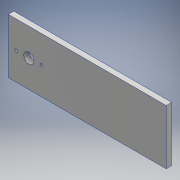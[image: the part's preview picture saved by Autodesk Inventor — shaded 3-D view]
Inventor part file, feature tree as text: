
AUTODESK INVENTOR PART (.ipt)
format: ipt  version: 2016 (Build 200138000, 138)  size: 115,200 bytes
history: native  units: mm
features: extrude x2, sketch x2, other x1
ambient origin geometry x8: Origin, YZ Plane, XZ Plane, XY Plane, X Axis, Y Axis, Z Axis, Center Point
bodies: Body1 (feature_tree)
feature tree (5):
  other  "ソリッド1"
  extrude  "押し出し1"  Depth=230.0mm
  extrude  "押し出し2"  Depth=80.0mm
  sketch  "スケッチ1"
  sketch  "スケッチ2"
